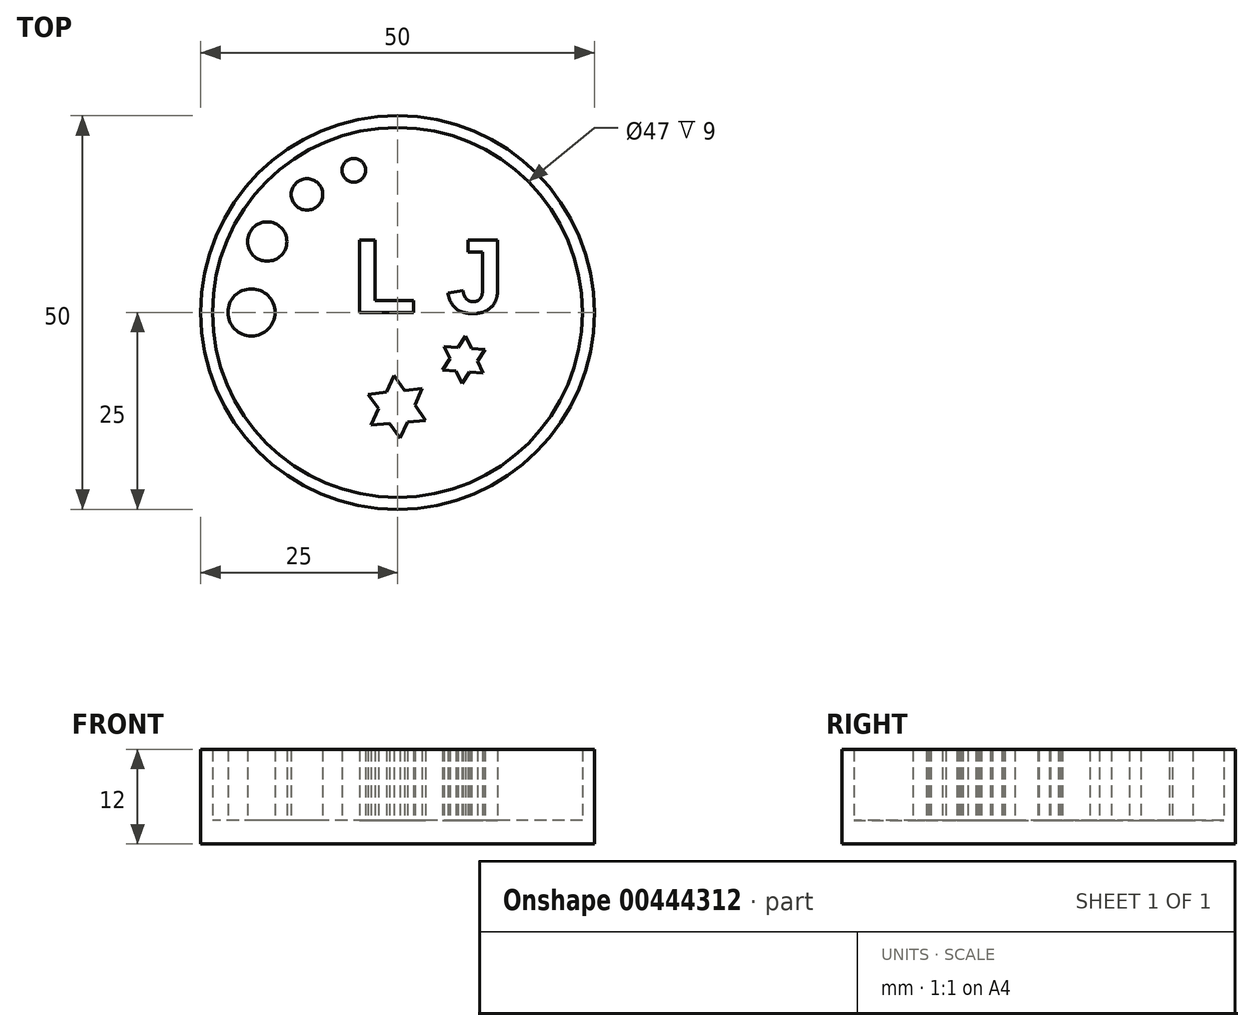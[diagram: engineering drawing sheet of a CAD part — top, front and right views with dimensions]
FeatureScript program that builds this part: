
annotation { "Feature Type Name" : "Feature", "Feature Type Description" : "" }
export const myFeature = defineFeature(function(context is Context, id is Id, definition is map)
    precondition{}
    {
        {
            var Q0;
            Q0=qCreatedBy(makeId("Top.planeOp"),FACE);
            var sketch = newSketch(context, id + "F0", { "sketchPlane" : qUnion([Q0])});
            skCircle(sketch, "E0", {"center": v(0, 0) * mm, "radius": 25 * mm});
            skSolve(sketch);
        }
        {
            var Q0;
            Q0=qCreatedBy(makeId("Top.planeOp"),FACE);
            var sketch = newSketch(context, id + "F1", { "sketchPlane" : qUnion([Q0])});
            skCircle(sketch, "E1", {"center": v(-18.55, 0) * mm, "radius": 3 * mm});
            skCircle(sketch, "E2", {"center": v(-16.55, 9.01) * mm, "radius": 2.5 * mm});
            skCircle(sketch, "E3", {"center": v(-11.5, 15) * mm, "radius": 2 * mm});
            skCircle(sketch, "E4", {"center": v(-5.55, 18.06) * mm, "radius": 1.5 * mm});
            skText(sketch, "E5", { "text": "L J", "fontName": "Arimo-Bold.ttf"});
            skCircle(sketch, "E6.cCircle", {"center": v(-0.08, -12) * mm, "radius": 4 * mm, "construction": true});
            skLineSegment(sketch, "E6.0", {"start": v(3.54, -13.7) * mm, "end": v(1.27, -13.9) * mm});
            skLineSegment(sketch, "E6.1", {"start": v(-3.36, -14.29) * mm, "end": v(-2.4, -12.23) * mm});
            skLineSegment(sketch, "E6.2", {"start": v(-0.42, -8.01) * mm, "end": v(0.88, -9.88) * mm});
            skLineSegment(sketch, "E7.0", {"start": v(3.14, -9.63) * mm, "end": v(2.2, -11.78) * mm});
            skLineSegment(sketch, "E7.1", {"start": v(0.35, -15.98) * mm, "end": v(-1.03, -14.09) * mm});
            skLineSegment(sketch, "E7.2", {"start": v(-3.74, -10.39) * mm, "end": v(-1.42, -10.13) * mm});
            skLineSegment(sketch, "E8.trimOffspring", {"start": v(0.88, -9.88) * mm, "end": v(3.14, -9.63) * mm});
            skLineSegment(sketch, "E9.trimOffspring", {"start": v(-1.42, -10.13) * mm, "end": v(-0.42, -8.01) * mm});
            skLineSegment(sketch, "E10.trimOffspring", {"start": v(-2.4, -12.23) * mm, "end": v(-3.74, -10.39) * mm});
            skLineSegment(sketch, "E11.trimOffspring", {"start": v(-1.03, -14.09) * mm, "end": v(-3.36, -14.29) * mm});
            skLineSegment(sketch, "E12.trimOffspring", {"start": v(1.27, -13.9) * mm, "end": v(0.35, -15.98) * mm});
            skLineSegment(sketch, "E13.trimOffspring", {"start": v(2.2, -11.78) * mm, "end": v(3.54, -13.7) * mm});
            skCircle(sketch, "E14.cCircle", {"center": v(8.42, -6) * mm, "radius": 3 * mm, "construction": true});
            skLineSegment(sketch, "E14.0", {"start": v(10.9, -7.7) * mm, "end": v(9.17, -7.57) * mm});
            skLineSegment(sketch, "E14.1", {"start": v(5.71, -7.3) * mm, "end": v(6.7, -5.87) * mm});
            skLineSegment(sketch, "E14.2", {"start": v(8.65, -3.02) * mm, "end": v(9.4, -4.58) * mm});
            skLineSegment(sketch, "E15.0", {"start": v(11.13, -4.71) * mm, "end": v(10.15, -6.14) * mm});
            skLineSegment(sketch, "E15.1", {"start": v(8.19, -9) * mm, "end": v(7.44, -7.44) * mm});
            skLineSegment(sketch, "E15.2", {"start": v(5.94, -4.31) * mm, "end": v(7.67, -4.44) * mm});
            skLineSegment(sketch, "E16.trimOffspring", {"start": v(9.4, -4.58) * mm, "end": v(11.13, -4.71) * mm});
            skLineSegment(sketch, "E17.trimOffspring", {"start": v(7.67, -4.44) * mm, "end": v(8.65, -3.02) * mm});
            skLineSegment(sketch, "E18.trimOffspring", {"start": v(6.7, -5.87) * mm, "end": v(5.94, -4.31) * mm});
            skLineSegment(sketch, "E19.trimOffspring", {"start": v(7.44, -7.44) * mm, "end": v(5.71, -7.3) * mm});
            skLineSegment(sketch, "E20.trimOffspring", {"start": v(9.17, -7.57) * mm, "end": v(8.19, -9) * mm});
            skLineSegment(sketch, "E21.trimOffspring", {"start": v(10.15, -6.14) * mm, "end": v(10.9, -7.7) * mm});
            skPoint(sketch, "E22", {"position": v(-0.05, 0) * mm});
            const initialGuessF1  = {"E5": [-0.0057, 0, 1, 0, 0.00964]};
            skSetInitialGuess(sketch, initialGuessF1);
            skSolve(sketch);
        }
        {
            var Q0;
            Q0=makeQuery(id+"F0.imprint","IMPRINT",FACE,{"disambiguationData":[TD([[makeQuery(id+"F0.imprint","IMPRINT",EDGE,{"derivedFrom":sQuery(id+"F0.wireOp",EDGE,"E0")}),1.0]])]});
            extrude(context, id + "F2", {"entities" : qUnion([Q0]), "oppositeDirection" : true, "depth" : 3 * mm});
        }
        {
            var Q0;
            Q0=qCreatedBy(makeId("Top.planeOp"),FACE);
            var sketch = newSketch(context, id + "F3", { "sketchPlane" : qUnion([Q0])});
            skCircle(sketch, "E23", {"center": v(0, 0) * mm, "radius": 25 * mm});
            skCircle(sketch, "E24", {"center": v(0, 0) * mm, "radius": 23.5 * mm});
            skSolve(sketch);
        }
        {
            var Q0;
            Q0=makeQuery(id+"F3.imprint","IMPRINT",FACE,{"disambiguationData":[TD([[makeQuery(id+"F3.imprint","IMPRINT",EDGE,{"derivedFrom":sQuery(id+"F3.wireOp",EDGE,"E23")}),1.0]])]});
            extrude(context, id + "F4", {"entities" : qUnion([Q0]), "operationType" : NewBodyOperationType.ADD, "depth" : 9 * mm});
        }
        {
            var Q0;
            Q0 = qSketchRegion(id + "F1", true);
            var Q1;
            Q1=makeQuery(id+"F4.opExtrude","CAP_FACE",FACE,{"disambiguationData":[OSD([sQuery(id+"F3.wireOp",EDGE,"E23"),sQuery(id+"F3.wireOp",EDGE,"E24")])],"isStart":false});
            extrude(context, id + "F5", {"entities" : qUnion([Q0]), "operationType" : NewBodyOperationType.ADD, "endBound" : BoundingType.UP_TO_SURFACE, "endBoundEntityFace" : qUnion([Q1]), "depth" : 25 * mm});
        }
    });
